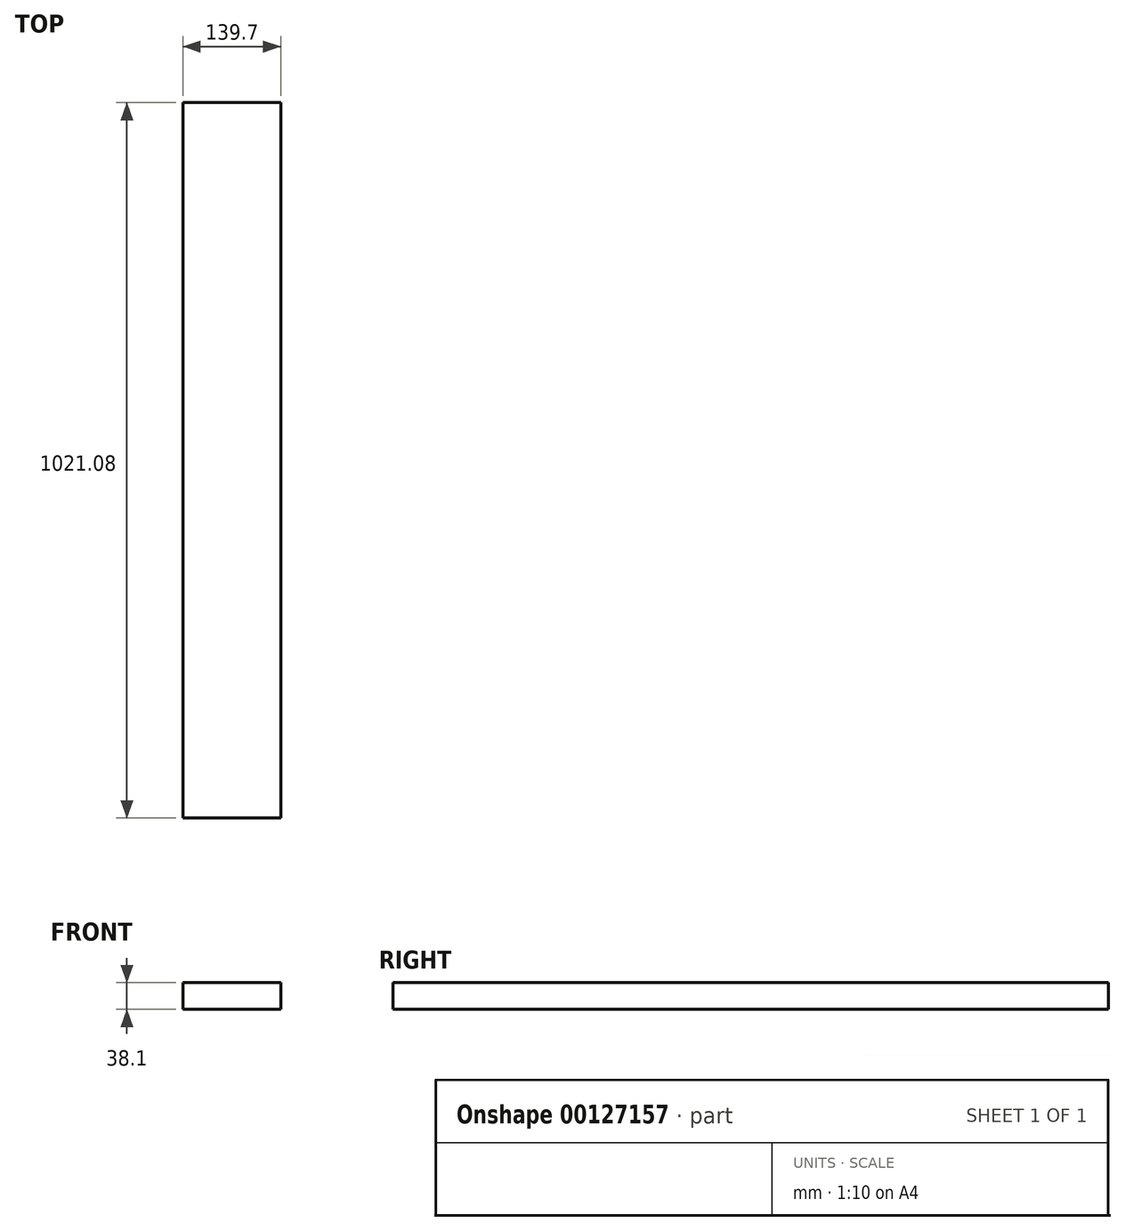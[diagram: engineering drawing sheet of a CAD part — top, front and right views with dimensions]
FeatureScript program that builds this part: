
annotation { "Feature Type Name" : "Feature", "Feature Type Description" : "" }
export const myFeature = defineFeature(function(context is Context, id is Id, definition is map)
    precondition{}
    {
        {
            var Q0;
            Q0=qCreatedBy(makeId("Front.planeOp"),FACE);
            var sketch = newSketch(context, id + "F0", { "sketchPlane" : qUnion([Q0])});
            skLineSegment(sketch, "E0.bottom", {"start": v(69.85, -19.05) * mm, "end": v(-69.85, -19.05) * mm});
            skLineSegment(sketch, "E0.top", {"start": v(69.85, 19.05) * mm, "end": v(-69.85, 19.05) * mm});
            skLineSegment(sketch, "E0.left", {"start": v(69.85, -19.05) * mm, "end": v(69.85, 19.05) * mm});
            skLineSegment(sketch, "E0.right", {"start": v(-69.85, -19.05) * mm, "end": v(-69.85, 19.05) * mm});
            skPoint(sketch, "E0.middle", {"position": v(0, 0) * mm});
            skSolve(sketch);
        }
        {
            var Q0;
            Q0=qSketchRegion(id+"F0",true);
            extrude(context, id + "F1", {"entities" : qUnion([Q0]), "depth" : 1021.08 * mm, "offsetDistance" : 25.4 * mm});
        }
    });
